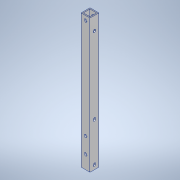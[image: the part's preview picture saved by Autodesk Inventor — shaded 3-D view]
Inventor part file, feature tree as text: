
AUTODESK INVENTOR PART (.ipt)
format: ipt  version: 2020.3 (Build 243373000, 373)  size: 148,992 bytes
history: native  units: mm
features: sketch x6, hole x5, other x1, extrude x1
ambient origin geometry x8: Origin, YZ Plane, XZ Plane, XY Plane, X Axis, Y Axis, Z Axis, Center Point
bodies: Body1 (feature_tree)
feature tree (13):
  other  "ソリッド1"
  extrude  "押し出し1"  Depth=9.0mm
  hole  "穴1"  [1 undecoded]
  hole  "穴2"  [1 undecoded]
  hole  "穴3"  [1 undecoded]
  hole  "穴4"  [1 undecoded]
  hole  "穴5"  [1 undecoded]
  sketch  "スケッチ1"
  sketch  "スケッチ2"
  sketch  "スケッチ3"
  sketch  "スケッチ4"
  sketch  "スケッチ5"
  sketch  "スケッチ6"
note: 5 required parameter values undecoded (feature->parameter linkage not recoverable at this tier; creation-order binding heuristic only, values carry confidence <= 0.55)
